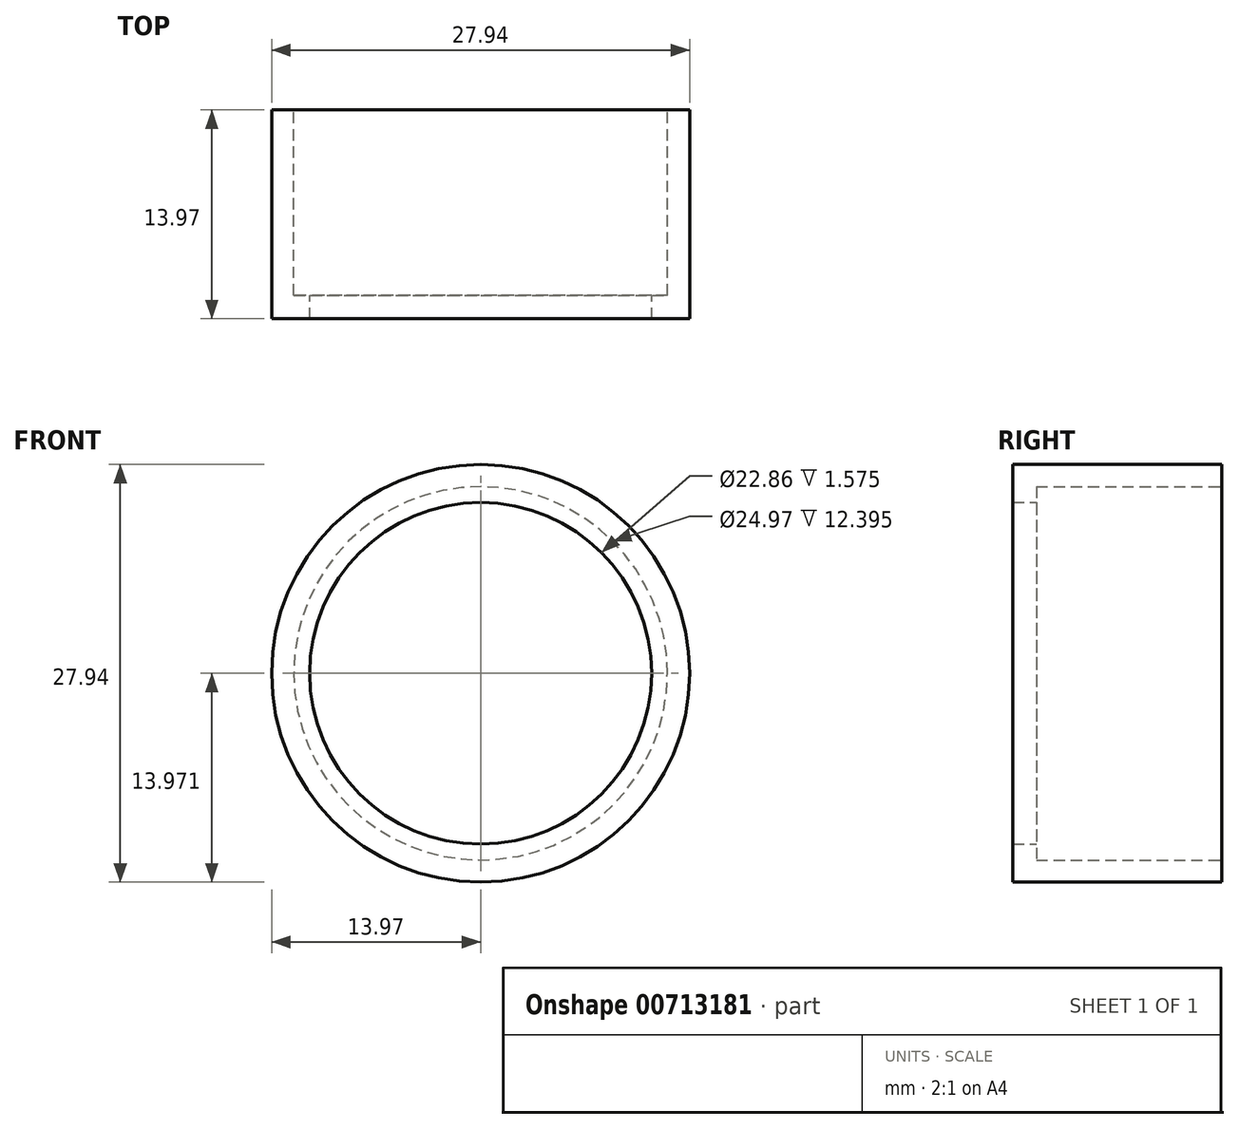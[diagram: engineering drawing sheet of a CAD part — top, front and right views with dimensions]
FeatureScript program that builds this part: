
annotation { "Feature Type Name" : "Feature", "Feature Type Description" : "" }
export const myFeature = defineFeature(function(context is Context, id is Id, definition is map)
    precondition{}
    {
        {
            var Q0;
            Q0=qCreatedBy(makeId("Front.planeOp"),FACE);
            var sketch = newSketch(context, id + "F0", { "sketchPlane" : qUnion([Q0])});
            skCircle(sketch, "E0", {"center": v(-146.3, 69.11) * mm, "radius": 13.97 * mm});
            skCircle(sketch, "E1", {"center": v(-146.3, 69.11) * mm, "radius": 11.43 * mm});
            skSolve(sketch);
        }
        {
            var Q0;
            Q0=makeQuery(id+"F0.imprint","IMPRINT",FACE,{"disambiguationData":[TD([[makeQuery(id+"F0.imprint","IMPRINT",EDGE,{"derivedFrom":sQuery(id+"F0.wireOp",EDGE,"E0")}),1.0]])]});
            extrude(context, id + "F1", {"entities" : qUnion([Q0]), "depth" : 13.97 * mm, "offsetDistance" : 25.4 * mm});
        }
        {
            var Q0;
            Q0=makeQuery(id+"F1.opExtrude","CAP_FACE",FACE,{"disambiguationData":[OSD([sQuery(id+"F0.wireOp",EDGE,"E0"),sQuery(id+"F0.wireOp",EDGE,"E1")])],"isStart":true});
            var sketch = newSketch(context, id + "F2", { "sketchPlane" : qUnion([Q0])});
            skCircle(sketch, "E2", {"center": v(146.3, 69.11) * mm, "radius": 12.48 * mm});
            skSolve(sketch);
        }
        {
            var Q0;
            Q0 = qSketchRegion(id + "F2", true);
            extrude(context, id + "F3", {"entities" : qUnion([Q0]), "operationType" : NewBodyOperationType.REMOVE, "oppositeDirection" : true, "depth" : 12.4 * mm, "offsetDistance" : 25.4 * mm});
        }
    });
